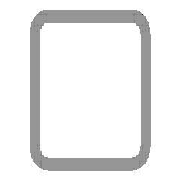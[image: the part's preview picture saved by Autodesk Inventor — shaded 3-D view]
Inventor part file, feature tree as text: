
AUTODESK INVENTOR PART (.ipt)
format: ipt  version: 2025 (Build 290162010, 162A)  size: 135,680 bytes
history: native  units: mm (DEFAULTED — no unit token found)
features: other x4, sketch x1, plane x1
ambient origin geometry x8: Origin, YZ Plane, XZ Plane, XY Plane, X Axis, Y Axis, Z Axis, Center Point
bodies: Solid1 (feature_tree), Body (feature_tree)
feature tree (6):
  parser-record x1  (decoder bookkeeping rows leaked as tree rows — omitted from the tree; the rows remain in map.json)
  other  "Driven Length"
  other  "Start plane"
  other  "End plane"
  sketch  "Sketch3"  dims[d3=2600.0mm d4=0.0mm d7=6.0mm d9=80.0mm d11=80.0mm d12=3.0mm d13=-0.0mm d14=2600.0mm d15=40.0mm d16=40.0mm d17=90.0deg d18=2600.0mm]
  plane  "Work Plane3"
